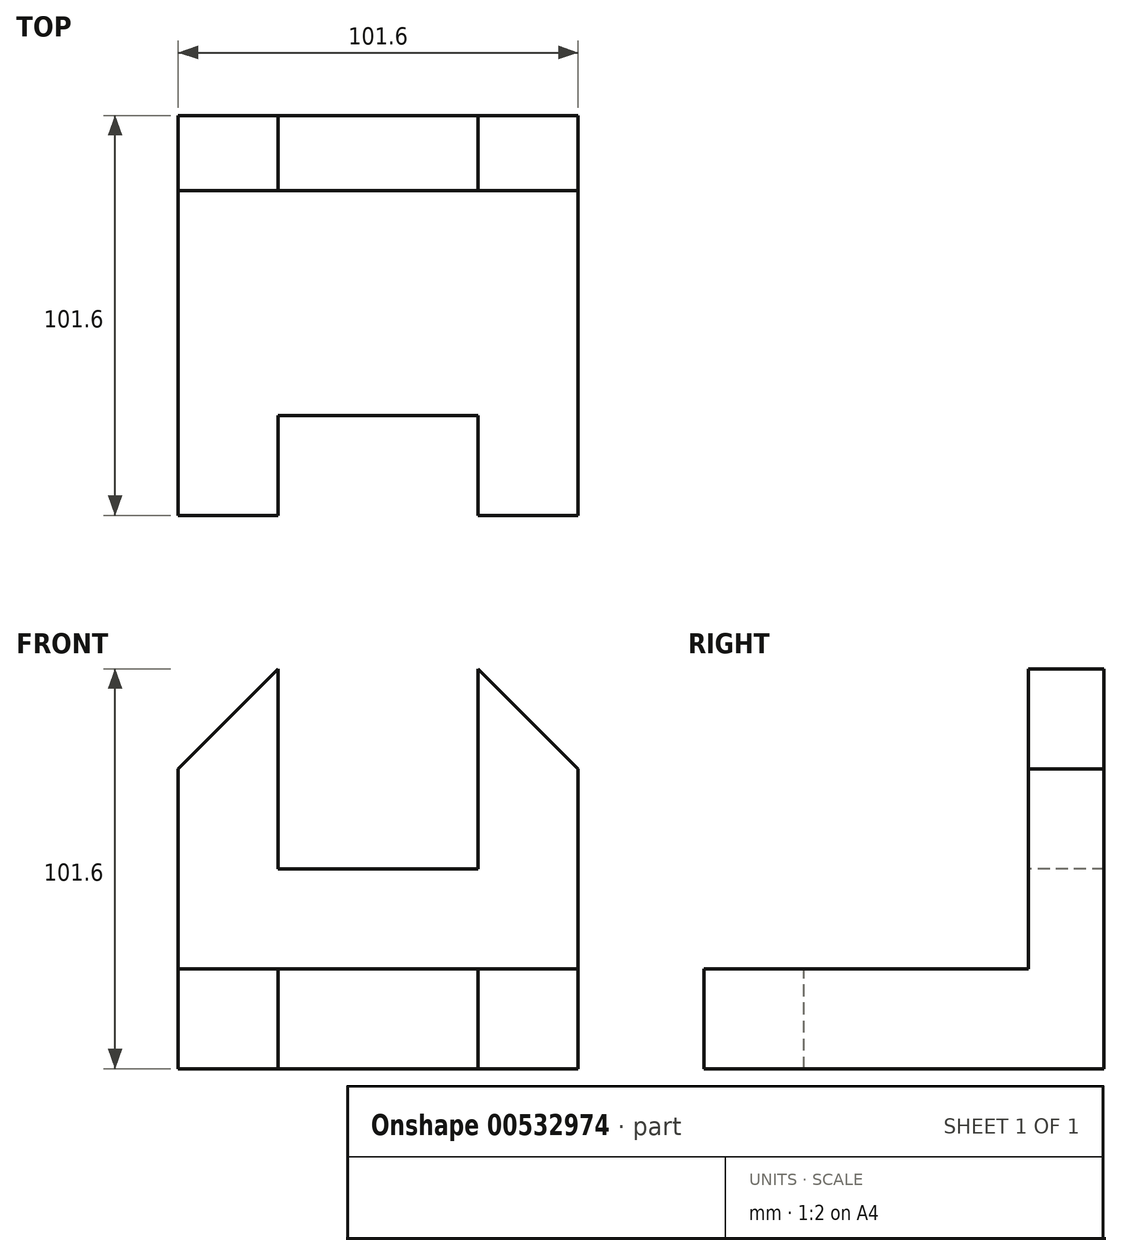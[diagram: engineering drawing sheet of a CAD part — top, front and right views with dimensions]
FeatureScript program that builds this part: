
annotation { "Feature Type Name" : "Feature", "Feature Type Description" : "" }
export const myFeature = defineFeature(function(context is Context, id is Id, definition is map)
    precondition{}
    {
        {
            var Q0;
            Q0=qCreatedBy(makeId("Front.planeOp"),FACE);
            var sketch = newSketch(context, id + "F0", { "sketchPlane" : qUnion([Q0])});
            skLineSegment(sketch, "E0.bottom", {"start": v(0, 0) * mm, "end": v(-101.6, 0) * mm});
            skLineSegment(sketch, "E0.top", {"start": v(0, -101.6) * mm, "end": v(-101.6, -101.6) * mm});
            skLineSegment(sketch, "E0.left", {"start": v(0, 0) * mm, "end": v(0, -101.6) * mm});
            skLineSegment(sketch, "E0.right", {"start": v(-101.6, 0) * mm, "end": v(-101.6, -101.6) * mm});
            skSolve(sketch);
        }
        {
            var Q0;
            Q0 = qSketchRegion(id + "F0", true);
            extrude(context, id + "F1", {"entities" : qUnion([Q0]), "depth" : 101.6 * mm, "offsetDistance" : 25.4 * mm});
        }
        {
            var Q0;
            Q0=makeQuery(id+"F1.opExtrude","SWEPT_FACE",FACE,{"disambiguationData":[OSD([sQuery(id+"F0.wireOp",EDGE,"E0.bottom")])]});
            var sketch = newSketch(context, id + "F2", { "sketchPlane" : qUnion([Q0])});
            skLineSegment(sketch, "E1.bottom", {"start": v(0, 0) * mm, "end": v(-101.6, 0) * mm});
            skLineSegment(sketch, "E1.top", {"start": v(0, -19.15) * mm, "end": v(-101.6, -19.15) * mm});
            skLineSegment(sketch, "E1.left", {"start": v(0, 0) * mm, "end": v(0, -19.15) * mm});
            skLineSegment(sketch, "E1.right", {"start": v(-101.6, 0) * mm, "end": v(-101.6, -19.15) * mm});
            skSolve(sketch);
        }
        {
            var Q0;
            {var subQ0=sQuery(id+"F2.wireOp",EDGE,"E1.top");Q0=makeQuery(id+"F2.imprint","IMPRINT",FACE,{"disambiguationData":[TD([[makeQuery(id+"F2.imprint","IMPRINT",EDGE,{"derivedFrom":subQ0}),1.0]])]});}
            extrude(context, id + "F3", {"entities" : qUnion([Q0]), "operationType" : NewBodyOperationType.REMOVE, "oppositeDirection" : true, "depth" : 76.2 * mm, "offsetDistance" : 25.4 * mm});
        }
        {
            var Q0;
            Q0=makeQuery(id+"F3.boolean.opBoolean","COPY",FACE,{"derivedFrom":makeQuery(id+"F3.opExtrude","CAP_FACE",FACE,{"disambiguationData":[OSD([sQuery(id+"F0.wireOp",EDGE,"E0.bottom"),sQuery(id+"F0.wireOp",EDGE,"E0.left"),sQuery(id+"F0.wireOp",EDGE,"E0.right"),sQuery(id+"F2.wireOp",EDGE,"E1.top")])],"isStart":false})});
            var sketch = newSketch(context, id + "F4", { "sketchPlane" : qUnion([Q0])});
            skLineSegment(sketch, "E2", {"start": v(-101.6, -101.6) * mm, "end": v(-101.6, -76.2) * mm});
            skLineSegment(sketch, "E3", {"start": v(-101.6, -76.2) * mm, "end": v(-76.2, -76.2) * mm});
            skLineSegment(sketch, "E4", {"start": v(-76.2, -76.2) * mm, "end": v(-76.2, -101.6) * mm});
            skLineSegment(sketch, "E5", {"start": v(-76.2, -76.2) * mm, "end": v(-25.4, -76.2) * mm});
            skLineSegment(sketch, "E6", {"start": v(-25.4, -76.2) * mm, "end": v(-25.4, -101.6) * mm});
            skSolve(sketch);
        }
        {
            var Q0;
            {var subQ0=sQuery(id+"F4.wireOp",EDGE,"E4");Q0=makeQuery(id+"F4.imprint","IMPRINT",FACE,{"disambiguationData":[TD([[makeQuery(id+"F4.imprint","IMPRINT",EDGE,{"derivedFrom":subQ0}),1.0]])]});}
            extrude(context, id + "F5", {"entities" : qUnion([Q0]), "operationType" : NewBodyOperationType.REMOVE, "oppositeDirection" : true, "depth" : 50.55 * mm, "offsetDistance" : 25.4 * mm});
        }
        {
            var Q0;
            Q0=makeQuery(id+"F1.opExtrude","SWEPT_FACE",FACE,{"disambiguationData":[OSD([sQuery(id+"F0.wireOp",EDGE,"E0.bottom")])]});
            var sketch = newSketch(context, id + "F6", { "sketchPlane" : qUnion([Q0])});
            skLineSegment(sketch, "E7.bottom", {"start": v(-101.6, 0) * mm, "end": v(-76.2, 0) * mm});
            skLineSegment(sketch, "E7.top", {"start": v(-101.6, -19.15) * mm, "end": v(-76.2, -19.15) * mm});
            skLineSegment(sketch, "E7.left", {"start": v(-101.6, 0) * mm, "end": v(-101.6, -19.15) * mm});
            skLineSegment(sketch, "E7.right", {"start": v(-76.2, 0) * mm, "end": v(-76.2, -19.15) * mm});
            skLineSegment(sketch, "E8.bottom", {"start": v(0, 0) * mm, "end": v(-25.4, 0) * mm});
            skLineSegment(sketch, "E8.top", {"start": v(0, -19.15) * mm, "end": v(-25.4, -19.15) * mm});
            skLineSegment(sketch, "E8.left", {"start": v(0, 0) * mm, "end": v(0, -19.15) * mm});
            skLineSegment(sketch, "E8.right", {"start": v(-25.4, 0) * mm, "end": v(-25.4, -19.15) * mm});
            skSolve(sketch);
        }
        {
            var Q0;
            {var subQ0=sQuery(id+"F6.wireOp",EDGE,"E7.right");Q0=makeQuery(id+"F6.imprint","IMPRINT",FACE,{"disambiguationData":[TD([[makeQuery(id+"F6.imprint","IMPRINT",EDGE,{"derivedFrom":subQ0}),1.0]])]});}
            extrude(context, id + "F7", {"entities" : qUnion([Q0]), "operationType" : NewBodyOperationType.REMOVE, "oppositeDirection" : true, "depth" : 50.8 * mm, "offsetDistance" : 25.4 * mm});
        }
        {
            var Q0;
            Q0=makeQuery(id+"F3.boolean.opBoolean","COPY",FACE,{"derivedFrom":makeQuery(id+"F3.opExtrude","SWEPT_FACE",FACE,{"disambiguationData":[OSD([sQuery(id+"F2.wireOp",EDGE,"E1.top")])]})});
            var sketch = newSketch(context, id + "F8", { "sketchPlane" : qUnion([Q0])});
            skLineSegment(sketch, "E9", {"start": v(0, -76.2) * mm, "end": v(0, -25.4) * mm});
            skLineSegment(sketch, "E10", {"start": v(-101.6, -76.2) * mm, "end": v(-101.6, -25.4) * mm});
            skLineSegment(sketch, "E11", {"start": v(-76.2, 0) * mm, "end": v(-101.6, -25.4) * mm});
            skLineSegment(sketch, "E12", {"start": v(-25.4, 0) * mm, "end": v(0, -25.4) * mm});
            skSolve(sketch);
        }
        {
            var Q0;
            Q0 = qSketchRegion(id + "F8", true);
            var Q1;
            {var subQ0=sQuery(id+"F8.wireOp",EDGE,"E11");Q1=makeQuery(id+"F8.imprint","IMPRINT",FACE,{"disambiguationData":[TD([[makeQuery(id+"F8.imprint","IMPRINT",EDGE,{"derivedFrom":subQ0}),-1.0]])]});}
            var Q2;
            {var subQ0=sQuery(id+"F8.wireOp",EDGE,"E12");Q2=makeQuery(id+"F8.imprint","IMPRINT",FACE,{"disambiguationData":[TD([[makeQuery(id+"F8.imprint","IMPRINT",EDGE,{"derivedFrom":subQ0}),1.0]])]});}
            extrude(context, id + "F9", {"entities" : qUnion([Q0, Q1, Q2]), "operationType" : NewBodyOperationType.REMOVE, "oppositeDirection" : true, "depth" : 136.9 * mm, "offsetDistance" : 25.4 * mm});
        }
    });
